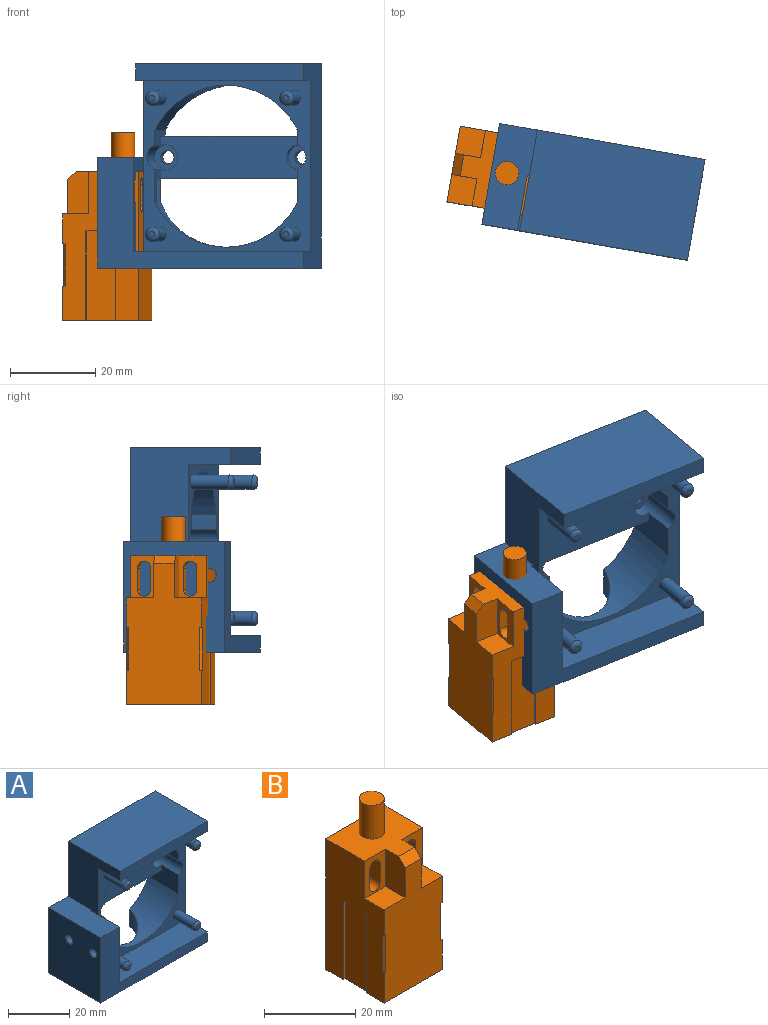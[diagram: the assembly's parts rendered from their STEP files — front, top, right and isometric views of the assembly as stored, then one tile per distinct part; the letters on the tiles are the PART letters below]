
ASSEMBLY  parts=2 mates=1
PART A: 58 faces, bbox 49x24x48 mm
  f0: plane 44.19x24mm, normal (-1,0,0), area 410.3mm2, adj f1,f3,f11,f12,f14,f16,f17,f18
  f1: plane 11.61x0.5mm, normal (0,-1,0), area 5.8mm2, adj f0,f4,f17,f54
  f2: plane 8.21x7.76mm, normal (1,0,0), area 34.7mm2, adj f10,f18,f22,f23,f25,f28,f51,f52
  f3: plane 5.3x0.5mm, normal (0,-1,0), area 2.7mm2, adj f0,f4,f51,f57
  f4: plane 22.19x13.13mm, normal (1,0,0), area 255.1mm2, adj f1,f3,f6,f17,f46,f47,f48,f49
  f5: cylinder r=1.6mm len=5.84mm, axis (-1,0,0), area 58.7mm2, adj f44,f56
  f6: plane 49x26mm, normal (0,-1,0), area 375.3mm2, adj f4,f13,f15,f17,f44,f57
  f7: plane 14x7.75mm, normal (-1,0,0), area 95.5mm2, adj f10,f11,f18,f22,f25,f26
  f8: plane 14x3.58mm, normal (-1,0,0), area 37mm2, adj f11,f18,f19,f24,f25,f26
  f9: plane 14x3.58mm, normal (1,0,0), area 37mm2, adj f11,f18,f19,f24,f25,f28
  f10: cylinder r=19mm len=34mm, axis (0,-1,0), area 314.6mm2, adj f2,f7,f11,f18,f23,f54
  f11: plane 49x48mm, normal (0,1,0), area 1145.5mm2, adj f0,f7,f8,f9,f10,f13,f14,f15
  f12: plane 40x3.99mm, normal (0,-1,0), area 159.6mm2, adj f0,f13,f14,f16
  f13: plane 48x24mm, normal (1,0,0), area 750mm2, adj f6,f11,f12,f14,f15,f16,f17,f18
  f14: plane 40x24mm, normal (0,0,1), area 960mm2, adj f0,f11,f12,f13
  f15: plane 49x24mm, normal (0,0,-1), area 929.4mm2, adj f6,f11,f13,f23,f44
  f16: plane 40x10mm, normal (0,0,-1), area 400mm2, adj f0,f12,f13,f18
  f17: plane 40.5x13.13mm, normal (0,0,1), area 406.6mm2, adj f0,f1,f4,f6,f13,f18
  f18: plane 40.2x40mm, normal (0,-1,0), area 467.1mm2, adj f0,f2,f7,f8,f9,f10,f13,f16
  f19: cylinder r=19mm len=34mm, axis (0,-1,0), area 541.3mm2, adj f8,f9,f11,f18,f20,f21
  f20: cylinder r=3mm len=8mm, axis (0,1,0), area 79.2mm2, adj f11,f19,f21
  f21: plane 6x3.24mm, normal (0,1,0), area 14.6mm2, adj f19,f20
  f22: plane 36.33x6mm, normal (0,0,-1), area 212.2mm2, adj f2,f7,f11,f23,f25
  f23: cylinder r=14mm len=27.65mm, axis (0,0,-1), area 373.2mm2, adj f2,f10,f11,f15,f22
  f24: plane 34x6mm, normal (0,0,1), area 204mm2, adj f8,f9,f11,f25
  f25: plane 34x10mm, normal (0,-1,0), area 299.7mm2, adj f2,f7,f8,f9,f22,f24,f26,f28
  f26: cylinder r=3mm len=11mm, axis (0,-1,0), area 115.3mm2, adj f7,f8,f18,f25,f27
  f27: plane 6x6mm, normal (0,-1,0), area 20.2mm2, adj f26,f30
  f28: cylinder r=3mm len=11mm, axis (0,-1,0), area 115.1mm2, adj f2,f9,f18,f25,f29
  f29: plane 6x6mm, normal (0,-1,0), area 20.2mm2, adj f28,f31
  f30: cylinder r=1.6mm len=3.2mm, axis (0,-1,0), area 30.2mm2, adj f11,f27
  f31: cylinder r=1.6mm len=3.2mm, axis (0,-1,0), area 30.2mm2, adj f11,f29
  f32: cylinder r=1.7mm len=9mm, axis (0,1,0), area 96.1mm2, adj f18,f43
  f33: plane 1.4x1.4mm, normal (0,-1,0), area 1.5mm2, adj f43
  f34: cylinder r=1.7mm len=9mm, axis (0,1,0), area 96.1mm2, adj f18,f42
  f35: plane 1.4x1.4mm, normal (0,-1,0), area 1.5mm2, adj f42
  f36: cylinder r=1.7mm len=9mm, axis (0,1,0), area 96.1mm2, adj f18,f40
  f37: plane 1.4x1.4mm, normal (0,-1,0), area 1.5mm2, adj f40
  f38: cylinder r=1.7mm len=9mm, axis (0,1,0), area 96.1mm2, adj f18,f41
  f39: plane 1.4x1.4mm, normal (0,-1,0), area 1.5mm2, adj f41
  f40: torus R=0.7mm, axis (0,-1,0), area 13.2mm2, adj f36,f37
  f41: torus R=0.7mm, axis (0,-1,0), area 13.2mm2, adj f38,f39
  f42: torus R=0.7mm, axis (0,-1,0), area 13.2mm2, adj f34,f35
  f43: torus R=0.7mm, axis (0,-1,0), area 13.2mm2, adj f32,f33
  f44: plane 26x24mm, normal (-1,0,0), area 607.9mm2, adj f5,f6,f11,f15,f45,f57
  f45: cylinder r=1.6mm len=4mm, axis (-1,0,0), area 40.2mm2, adj f44,f50
  f46: plane 5.4x4.5mm, normal (0,1,0), area 24.3mm2, adj f4,f47,f49,f50
  f47: plane 5.4x4.5mm, normal (0,0,-1), area 24.3mm2, adj f4,f46,f48,f50
  f48: plane 5.4x4.5mm, normal (0,-1,0), area 24.3mm2, adj f4,f47,f49,f50
  f49: plane 5.4x4.5mm, normal (0,0,1), area 24.3mm2, adj f4,f46,f48,f50
  f50: plane 5.4x5.4mm, normal (1,0,0), area 21.1mm2, adj f45,f46,f47,f48,f49
  f51: plane 6x5.4mm, normal (0,0,-1), area 31.7mm2, adj f0,f2,f3,f4,f52,f53,f55,f56
  f52: plane 5.27x2.84mm, normal (0,1,0), area 15mm2, adj f0,f2,f51,f54
  f53: plane 5.27x2.66mm, normal (0,1,0), area 14mm2, adj f4,f51,f54,f56
  f54: plane 6x5.4mm, normal (0,0,1), area 31.7mm2, adj f0,f1,f4,f10,f52,f53,f55,f56
  f55: plane 6x5.27mm, normal (0,-1,0), area 31.6mm2, adj f2,f51,f54,f56
  f56: plane 5.4x5.27mm, normal (1,0,0), area 20.4mm2, adj f5,f51,f53,f54,f55
  f57: plane 24x9mm, normal (0,0,1), area 209.4mm2, adj f0,f3,f4,f6,f11,f44
PART B: 37 faces, bbox 18x18x44 mm
  f0: plane 33x18mm, normal (0,-1,0), area 480mm2, adj f1,f2,f4,f8,f9,f10,f11,f20
  f1: plane 35x18mm, normal (-1,0,0), area 418mm2, adj f0,f3,f5,f7,f8,f11,f25,f26
  f2: plane 35x18mm, normal (1,0,0), area 418mm2, adj f0,f3,f5,f6,f8,f9,f21,f22
  f3: plane 18x16mm, normal (0,0,1), area 212.2mm2, adj f1,f2,f4,f5,f6,f7,f10,f20
  f4: plane 10x6mm, normal (1,0,0), area 58mm2, adj f0,f3,f6,f9,f20
  f5: plane 35x18mm, normal (0,1,0), area 581.9mm2, adj f1,f2,f3,f8,f12,f13,f14,f15
  f6: plane 10x6.5mm, normal (0,-1,0), area 41mm2, adj f2,f3,f4,f9,f16,f17,f18,f19
  f7: plane 10x6.5mm, normal (0,-1,0), area 41mm2, adj f1,f3,f10,f11,f12,f13,f14,f15
  f8: plane 18x18mm, normal (0,0,-1), area 317mm2, adj f0,f1,f2,f5,f21,f23,f24,f25
  f9: plane 6.5x6mm, normal (0,0,1), area 39mm2, adj f0,f2,f4,f6
  f10: plane 10x6mm, normal (-1,0,0), area 58mm2, adj f0,f3,f7,f11,f20
  f11: plane 6.5x6mm, normal (0,0,1), area 39mm2, adj f0,f1,f7,f10
  f12: plane 12x5mm, normal (-1,0,0), area 60mm2, adj f5,f7,f13,f15
  f13: cylinder r=1.6mm len=12mm, axis (0,-1,0), area 60.3mm2, adj f5,f7,f12,f14
  f14: plane 12x5mm, normal (1,0,0), area 60mm2, adj f5,f7,f13,f15
  f15: cylinder r=1.6mm len=12mm, axis (0,-1,0), area 60.3mm2, adj f5,f7,f12,f14
  f16: plane 12x5mm, normal (-1,0,0), area 60mm2, adj f5,f6,f17,f19
  f17: cylinder r=1.6mm len=12mm, axis (0,-1,0), area 60.3mm2, adj f5,f6,f16,f18
  f18: plane 12x5mm, normal (1,0,0), area 60mm2, adj f5,f6,f17,f19
  f19: cylinder r=1.6mm len=12mm, axis (0,-1,0), area 60.3mm2, adj f5,f6,f16,f18
  f20: plane 5x2mm, normal (0,-0.71,0.71), area 14.1mm2, adj f0,f3,f4,f10
  f21: plane 21x0.5mm, normal (0,-1,0), area 10.5mm2, adj f2,f8,f22,f24
  f22: plane 7x0.5mm, normal (0,0,-1), area 3.5mm2, adj f2,f21,f23,f24
  f23: plane 21x0.5mm, normal (0,1,0), area 10.5mm2, adj f2,f8,f22,f24
  f24: plane 21x7mm, normal (1,0,0), area 147mm2, adj f8,f21,f22,f23
  f25: plane 21x0.5mm, normal (0,1,0), area 10.5mm2, adj f1,f8,f26,f28
  f26: plane 7x0.5mm, normal (0,0,-1), area 3.5mm2, adj f1,f25,f27,f28
  f27: plane 21x0.5mm, normal (0,-1,0), area 10.5mm2, adj f1,f8,f26,f28
  f28: plane 21x7mm, normal (-1,0,0), area 147mm2, adj f8,f25,f26,f27
  f29: cylinder r=2.75mm len=9mm, axis (0,0,-1), area 155.5mm2, adj f3,f30
  f30: plane 5.5x5.5mm, normal (0,0,1), area 23.8mm2, adj f29
  f31: plane 10x0.5mm, normal (0.71,-0.71,0), area 7.1mm2, adj f0,f2,f32,f33
  f32: plane 0.5x0.5mm, normal (0,0,-1), area 0.1mm2, adj f0,f2,f31
  f33: plane 0.5x0.5mm, normal (0,0,1), area 0.1mm2, adj f0,f2,f31
  f34: plane 10x0.5mm, normal (-0.71,-0.71,0), area 7.1mm2, adj f0,f1,f35,f36
  f35: plane 0.5x0.5mm, normal (0,0,-1), area 0.1mm2, adj f0,f1,f34
  f36: plane 0.5x0.5mm, normal (0,0,1), area 0.1mm2, adj f0,f1,f34
PLACE A rot(axis=(0,0,-1),10deg) t=(14,-13.61,9.25)mm
PLACE B rot(axis=(0,0,-1),100deg) t=(-7.48,-21.21,-6.87)mm
MATE planar B.f5 <-> A.f0  axis (0.98,-0.17,0) through (-7.49,-21.24,-12.52)mm
